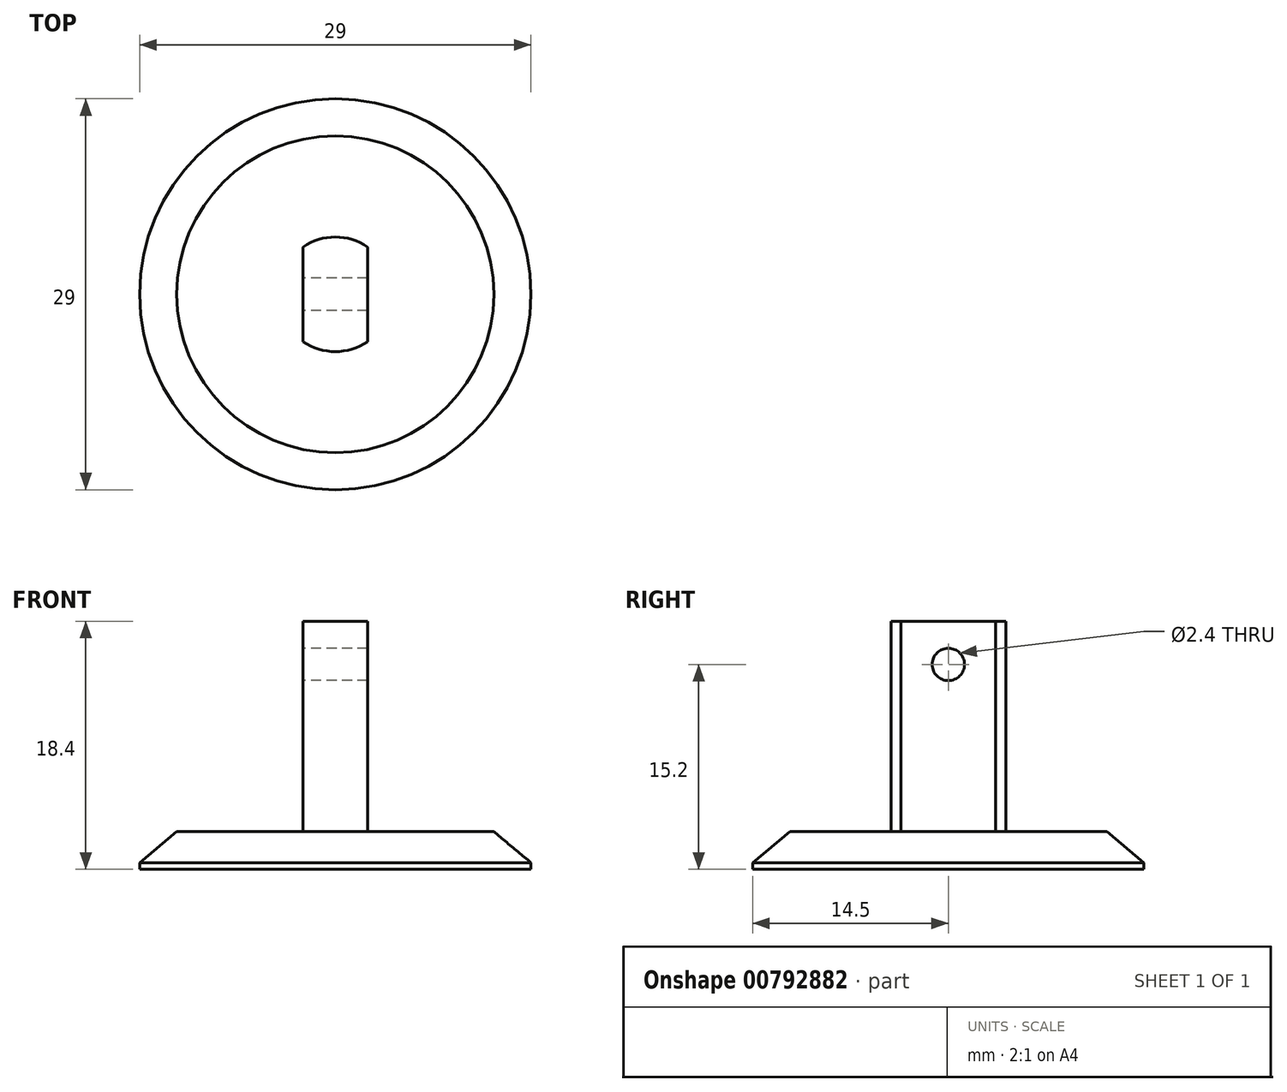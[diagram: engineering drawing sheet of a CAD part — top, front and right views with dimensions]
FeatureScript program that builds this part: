
annotation { "Feature Type Name" : "Feature", "Feature Type Description" : "" }
export const myFeature = defineFeature(function(context is Context, id is Id, definition is map)
    precondition{}
    {
        {
            var Q0;
            Q0=qCreatedBy(makeId("Front.planeOp"),FACE);
            var sketch = newSketch(context, id + "F0", { "sketchPlane" : qUnion([Q0])});
            skLineSegment(sketch, "E0.bottom", {"start": v(0, 0) * mm, "end": v(4.25, 0) * mm});
            skLineSegment(sketch, "E0.top", {"start": v(0, 18.4) * mm, "end": v(4.25, 18.4) * mm});
            skLineSegment(sketch, "E0.left", {"start": v(0, 0) * mm, "end": v(0, 18.4) * mm});
            skLineSegment(sketch, "E0.right", {"start": v(4.25, 0) * mm, "end": v(4.25, 18.4) * mm});
            skLineSegment(sketch, "E1.bottom", {"start": v(0, 0) * mm, "end": v(14.5, 0) * mm});
            skLineSegment(sketch, "E1.top", {"start": v(0, 2.8) * mm, "end": v(14.5, 2.8) * mm});
            skLineSegment(sketch, "E1.left", {"start": v(0, 0) * mm, "end": v(0, 2.8) * mm});
            skLineSegment(sketch, "E1.right", {"start": v(14.5, 0) * mm, "end": v(14.5, 2.8) * mm});
            skLineSegment(sketch, "E2", {"start": v(0, 21.44) * mm, "end": v(0, -3.84) * mm, "construction": true});
            skSolve(sketch);
        }
        {
            var Q0;
            Q0 = qSketchRegion(id + "F0", true);
            var Q1;
            Q1=sQuery(id+"F0.wireOp",EDGE,"E2");
            revolve(context, id + "F1", {"surfaceOperationType" : NewSurfaceOperationType.NEW, "entities" : qUnion([Q0]), "axis" : qUnion([Q1]), "revolveType" : RevolveType.FULL});
        }
        {
            var Q0;
            Q0=qCreatedBy(makeId("Front.planeOp"),FACE);
            var sketch = newSketch(context, id + "F2", { "sketchPlane" : qUnion([Q0])});
            skLineSegment(sketch, "E3", {"start": v(0, 0) * mm, "end": v(0, 24) * mm, "construction": true});
            skLineSegment(sketch, "E4.0", {"start": v(-14.5, 2.8) * mm, "end": v(0, 2.8) * mm});
            skLineSegment(sketch, "E5.trimOffspring", {"start": v(11.75, 2.8) * mm, "end": v(14.5, 2.8) * mm});
            skLineSegment(sketch, "E6", {"start": v(14.5, 2.8) * mm, "end": v(14.5, 0.5) * mm});
            skLineSegment(sketch, "E7", {"start": v(14.5, 0.5) * mm, "end": v(11.75, 2.8) * mm});
            skSolve(sketch);
        }
        {
            var Q0;
            Q0 = qSketchRegion(id + "F2", true);
            var Q1;
            Q1=sQuery(id+"F2.wireOp",EDGE,"E3");
            revolve(context, id + "F3", {"operationType" : NewBodyOperationType.REMOVE, "surfaceOperationType" : NewSurfaceOperationType.NEW, "entities" : qUnion([Q0]), "axis" : qUnion([Q1]), "revolveType" : RevolveType.FULL, "oppositeDirection" : true});
        }
        {
            var Q0;
            Q0=makeQuery(id+"F1.opRevolve","SWEPT_FACE",FACE,{"disambiguationData":[OSD([sQuery(id+"F0.wireOp",EDGE,"E0.top")])]});
            var sketch = newSketch(context, id + "F4", { "sketchPlane" : qUnion([Q0])});
            skLineSegment(sketch, "E8.bottom", {"start": v(2.4, -4.25) * mm, "end": v(-2.4, -4.25) * mm, "construction": true});
            skLineSegment(sketch, "E8.top", {"start": v(2.4, 4.25) * mm, "end": v(-2.4, 4.25) * mm, "construction": true});
            skLineSegment(sketch, "E8.left", {"start": v(2.4, -4.25) * mm, "end": v(2.4, 4.25) * mm, "construction": true});
            skLineSegment(sketch, "E8.right", {"start": v(-2.4, -4.25) * mm, "end": v(-2.4, 4.25) * mm, "construction": true});
            skPoint(sketch, "E8.middle", {"position": v(0, 0) * mm});
            skLineSegment(sketch, "E9.bottom", {"start": v(2.4, 4.25) * mm, "end": v(7.2, 4.25) * mm});
            skLineSegment(sketch, "E9.top", {"start": v(2.4, -4.25) * mm, "end": v(7.2, -4.25) * mm});
            skLineSegment(sketch, "E9.left", {"start": v(2.4, 4.25) * mm, "end": v(2.4, -4.25) * mm});
            skLineSegment(sketch, "E9.right", {"start": v(7.2, 4.25) * mm, "end": v(7.2, -4.25) * mm});
            skLineSegment(sketch, "E10.bottom", {"start": v(-2.4, 4.25) * mm, "end": v(-7.2, 4.25) * mm});
            skLineSegment(sketch, "E10.top", {"start": v(-2.4, -4.25) * mm, "end": v(-7.2, -4.25) * mm});
            skLineSegment(sketch, "E10.left", {"start": v(-2.4, 4.25) * mm, "end": v(-2.4, -4.25) * mm});
            skLineSegment(sketch, "E10.right", {"start": v(-7.2, 4.25) * mm, "end": v(-7.2, -4.25) * mm});
            skSolve(sketch);
        }
        {
            var Q0;
            Q0 = qSketchRegion(id + "F4", true);
            var Q1;
            Q1=makeQuery(id+"F1.opRevolve","SWEPT_FACE",FACE,{"disambiguationData":[OSD([sQuery(id+"F0.wireOp",EDGE,"E1.top")])]});
            extrude(context, id + "F5", {"entities" : qUnion([Q0]), "operationType" : NewBodyOperationType.REMOVE, "endBound" : BoundingType.UP_TO_SURFACE, "oppositeDirection" : true, "depth" : 25 * mm, "endBoundEntityFace" : qUnion([Q1]), "offsetDistance" : 25 * mm});
        }
        {
            var Q0;
            Q0=makeQuery(id+"F5.boolean.opBoolean","COPY",FACE,{"derivedFrom":makeQuery(id+"F5.opExtrude","SWEPT_FACE",FACE,{"disambiguationData":[OSD([sQuery(id+"F4.wireOp",EDGE,"E10.left")])]})});
            var sketch = newSketch(context, id + "F6", { "sketchPlane" : qUnion([Q0])});
            skCircle(sketch, "E11", {"center": v(0, 15.2) * mm, "radius": 1.2 * mm});
            skPoint(sketch, "E11.centerSnap0", {"position": v(0, 18.4) * mm});
            skSolve(sketch);
        }
        {
            var Q0;
            Q0 = qSketchRegion(id + "F6", true);
            extrude(context, id + "F7", {"entities" : qUnion([Q0]), "operationType" : NewBodyOperationType.REMOVE, "endBound" : BoundingType.THROUGH_ALL, "oppositeDirection" : true, "depth" : 25 * mm, "offsetDistance" : 25 * mm});
        }
    });
